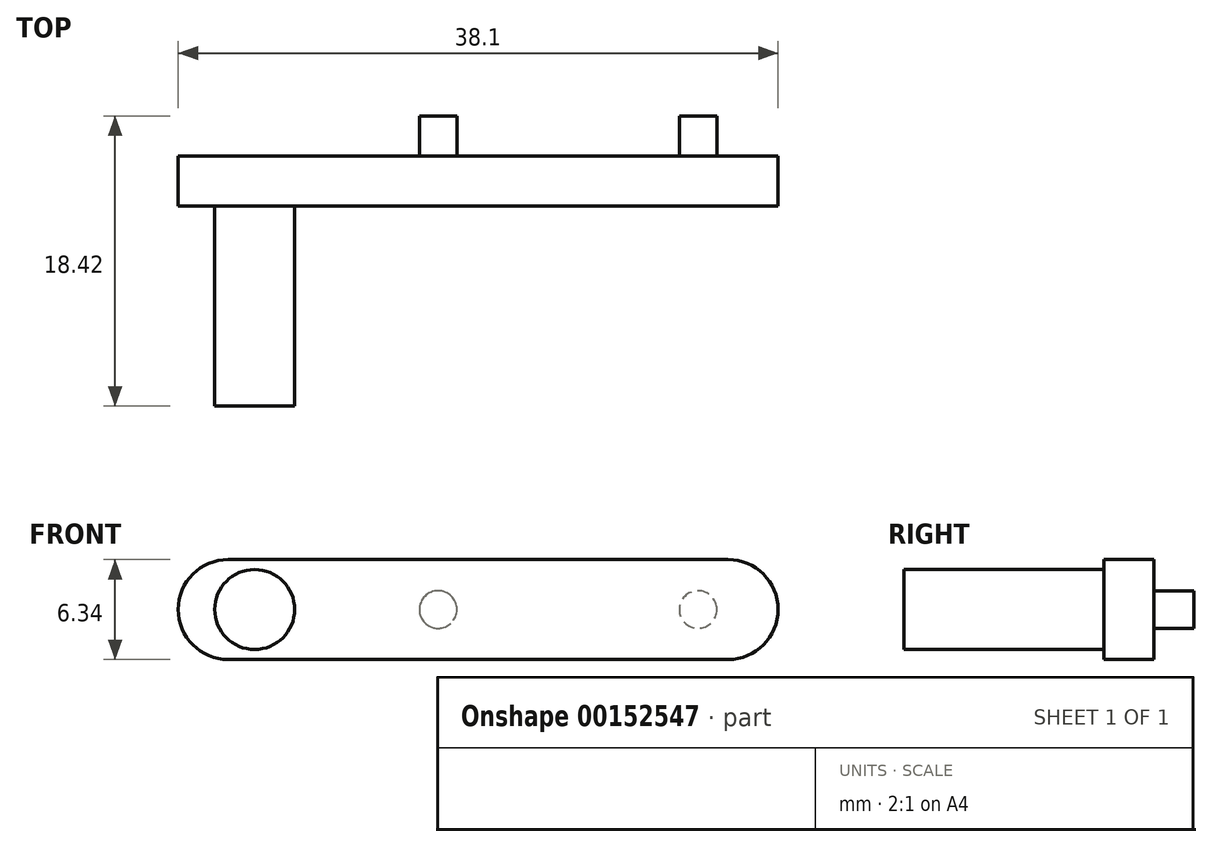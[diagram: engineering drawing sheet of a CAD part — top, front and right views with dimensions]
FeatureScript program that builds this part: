
annotation { "Feature Type Name" : "Feature", "Feature Type Description" : "" }
export const myFeature = defineFeature(function(context is Context, id is Id, definition is map)
    precondition{}
    {
        {
            var Q0;
            Q0=qCreatedBy(makeId("Front.planeOp"),FACE);
            var sketch = newSketch(context, id + "F0", { "sketchPlane" : qUnion([Q0])});
            skArc(sketch, "E0", {"start": v(-13.6, 3.18) * mm, "mid": v(-16.77, 0) * mm, "end": v(-13.6, -3.18) * mm});
            skArc(sketch, "E1", {"start": v(18.16, -3.18) * mm, "mid": v(21.33, 0) * mm, "end": v(18.16, 3.17) * mm});
            skLineSegment(sketch, "E2", {"start": v(-13.6, 3.18) * mm, "end": v(18.16, 3.17) * mm});
            skLineSegment(sketch, "E3", {"start": v(-13.6, -3.18) * mm, "end": v(18.16, -3.18) * mm});
            skSolve(sketch);
        }
        {
            var Q0;
            Q0 = qSketchRegion(id + "F0", true);
            extrude(context, id + "F1", {"entities" : qUnion([Q0]), "depth" : 3.17 * mm});
        }
        {
            var Q0;
            Q0=makeQuery(id+"F1.opExtrude","CAP_FACE",FACE,{"disambiguationData":[OSD([sQuery(id+"F0.wireOp",EDGE,"E0"),sQuery(id+"F0.wireOp",EDGE,"E1"),sQuery(id+"F0.wireOp",EDGE,"E2"),sQuery(id+"F0.wireOp",EDGE,"E3")])],"isStart":false});
            var sketch = newSketch(context, id + "F2", { "sketchPlane" : qUnion([Q0])});
            skCircle(sketch, "E4", {"center": v(-11.91, 0) * mm, "radius": 2.54 * mm});
            skPoint(sketch, "E4.centerSnap0", {"position": v(-16.77, 0) * mm});
            skSolve(sketch);
        }
        {
            var Q0;
            Q0 = qSketchRegion(id + "F2", true);
            extrude(context, id + "F3", {"entities" : qUnion([Q0]), "operationType" : NewBodyOperationType.ADD, "depth" : 12.7 * mm});
        }
        {
            var Q0;
            Q0=makeQuery(id+"F1.opExtrude","CAP_FACE",FACE,{"disambiguationData":[OSD([sQuery(id+"F0.wireOp",EDGE,"E0"),sQuery(id+"F0.wireOp",EDGE,"E1"),sQuery(id+"F0.wireOp",EDGE,"E2"),sQuery(id+"F0.wireOp",EDGE,"E3")])],"isStart":true});
            var sketch = newSketch(context, id + "F4", { "sketchPlane" : qUnion([Q0])});
            skCircle(sketch, "E5", {"center": v(-16.25, 0) * mm, "radius": 1.2 * mm});
            skCircle(sketch, "E6", {"center": v(0.26, 0) * mm, "radius": 1.2 * mm});
            skSolve(sketch);
        }
        {
            var Q0;
            Q0 = qSketchRegion(id + "F4", true);
            extrude(context, id + "F5", {"entities" : qUnion([Q0]), "operationType" : NewBodyOperationType.ADD, "depth" : 2.54 * mm});
        }
    });
